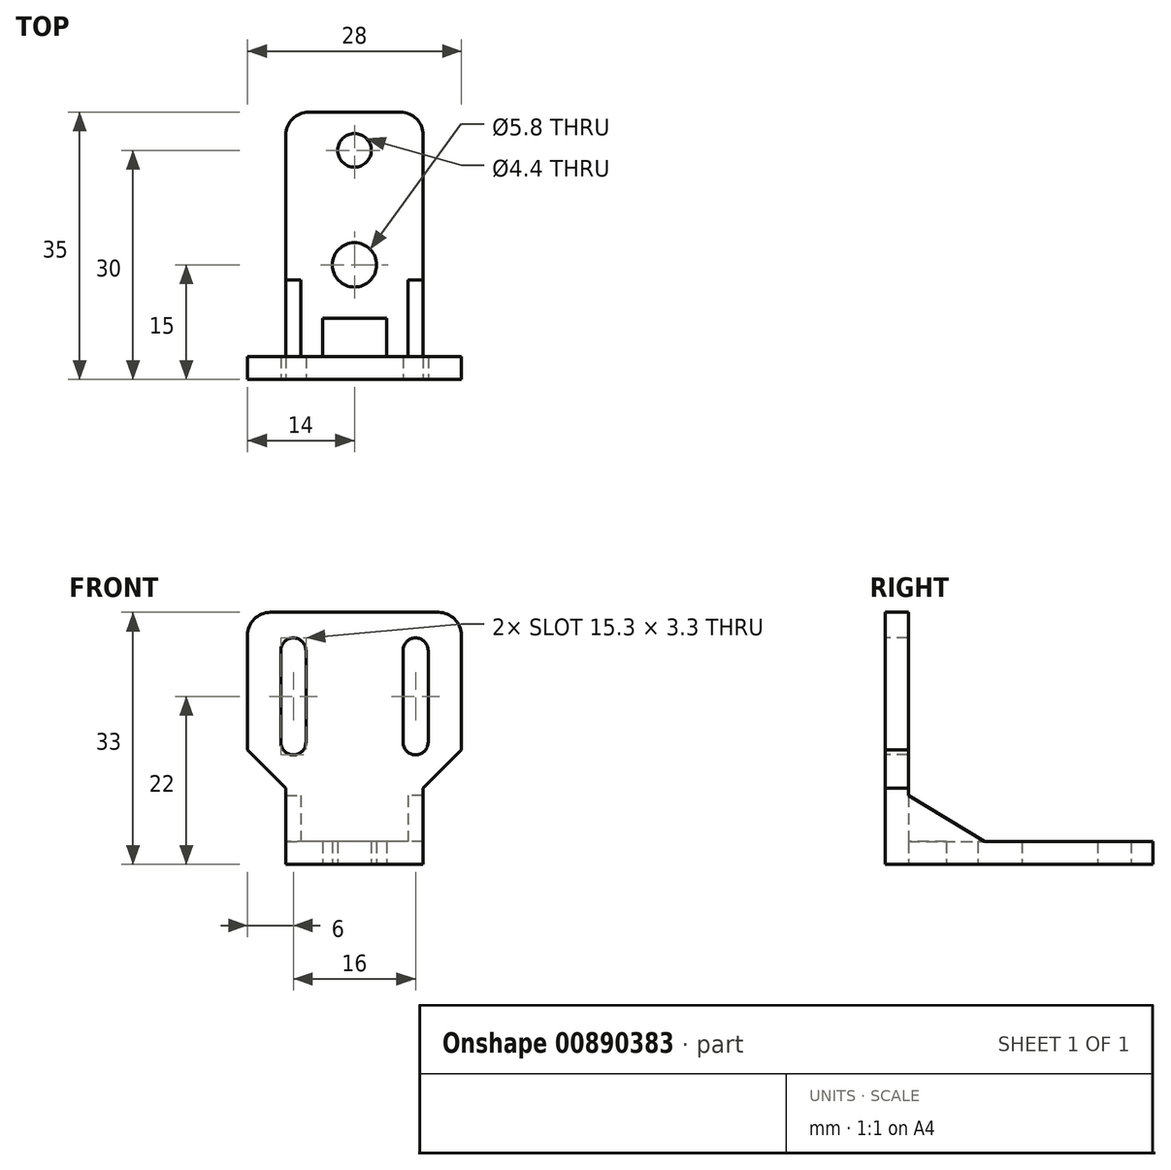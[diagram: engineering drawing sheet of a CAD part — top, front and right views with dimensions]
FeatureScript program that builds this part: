
annotation { "Feature Type Name" : "Feature", "Feature Type Description" : "" }
export const myFeature = defineFeature(function(context is Context, id is Id, definition is map)
    precondition{}
    {
        {
            var Q0;
            Q0=qCreatedBy(makeId("Top.planeOp"),FACE);
            var sketch = newSketch(context, id + "F0", { "sketchPlane" : qUnion([Q0])});
            skLineSegment(sketch, "E0.bottom", {"start": v(9, 17.5) * mm, "end": v(-9, 17.5) * mm});
            skLineSegment(sketch, "E0.top", {"start": v(9, -17.5) * mm, "end": v(-9, -17.5) * mm});
            skLineSegment(sketch, "E0.left", {"start": v(9, 17.5) * mm, "end": v(9, -17.5) * mm});
            skLineSegment(sketch, "E0.right", {"start": v(-9, 17.5) * mm, "end": v(-9, -17.5) * mm});
            skPoint(sketch, "E0.middle", {"position": v(0, 0) * mm});
            skCircle(sketch, "E1", {"center": v(0, 12.5) * mm, "radius": 2.2 * mm});
            skCircle(sketch, "E2", {"center": v(0, -2.5) * mm, "radius": 2.9 * mm});
            skLineSegment(sketch, "E3.bottom", {"start": v(4.2, -9.5) * mm, "end": v(-4.2, -9.5) * mm});
            skLineSegment(sketch, "E3.top", {"start": v(4.2, -14.5) * mm, "end": v(-4.2, -14.5) * mm});
            skLineSegment(sketch, "E3.left", {"start": v(4.2, -9.5) * mm, "end": v(4.2, -14.5) * mm});
            skLineSegment(sketch, "E3.right", {"start": v(-4.2, -9.5) * mm, "end": v(-4.2, -14.5) * mm});
            skPoint(sketch, "E3.middle", {"position": v(0, -12) * mm});
            skSolve(sketch);
        }
        {
            var Q0;
            Q0=makeQuery(id+"F0.imprint","IMPRINT",FACE,{"disambiguationData":[TD([[makeQuery(id+"F0.imprint","IMPRINT",EDGE,{"derivedFrom":sQuery(id+"F0.wireOp",EDGE,"E0.bottom")}),1.0]])]});
            extrude(context, id + "F1", {"entities" : qUnion([Q0]), "depth" : 3 * mm, "offsetDistance" : 25 * mm});
        }
        {
            var Q0;
            Q0=makeQuery(id+"F1.opExtrude","SWEPT_FACE",FACE,{"disambiguationData":[OSD([sQuery(id+"F0.wireOp",EDGE,"E0.top")])]});
            var sketch = newSketch(context, id + "F2", { "sketchPlane" : qUnion([Q0])});
            skLineSegment(sketch, "E4.bottom", {"start": v(-9, 0) * mm, "end": v(9, 0) * mm});
            skLineSegment(sketch, "E4.top", {"start": v(-9, 10) * mm, "end": v(9, 10) * mm});
            skLineSegment(sketch, "E4.left", {"start": v(-9, 0) * mm, "end": v(-9, 10) * mm});
            skLineSegment(sketch, "E4.right", {"start": v(9, 0) * mm, "end": v(9, 10) * mm});
            skLineSegment(sketch, "E5.bottom", {"start": v(14, 15) * mm, "end": v(-14, 15) * mm});
            skLineSegment(sketch, "E5.top", {"start": v(14, 33) * mm, "end": v(-14, 33) * mm});
            skLineSegment(sketch, "E5.left", {"start": v(14, 15) * mm, "end": v(14, 33) * mm});
            skLineSegment(sketch, "E5.right", {"start": v(-14, 15) * mm, "end": v(-14, 33) * mm});
            skPoint(sketch, "E5.middle", {"position": v(0, 24) * mm});
            skLineSegment(sketch, "E6", {"start": v(-14, 15) * mm, "end": v(-9, 10) * mm});
            skLineSegment(sketch, "E7", {"start": v(9, 10) * mm, "end": v(14, 15) * mm});
            skLineSegment(sketch, "E8", {"start": v(-8, 28) * mm, "end": v(-8, 16) * mm, "construction": true});
            skLineSegment(sketch, "E9.MirrorCS", {"start": v(8, 28) * mm, "end": v(8, 16) * mm, "construction": true});
            skArc(sketch, "E10.0.startCap", {"start": v(-9.65, 28) * mm, "mid": v(-8, 29.65) * mm, "end": v(-6.35, 28) * mm});
            skArc(sketch, "E10.0.endCap", {"start": v(-6.35, 16) * mm, "mid": v(-8, 14.35) * mm, "end": v(-9.65, 16) * mm});
            skLineSegment(sketch, "E10.0.left", {"start": v(-6.35, 28) * mm, "end": v(-6.35, 16) * mm});
            skLineSegment(sketch, "E10.0.right", {"start": v(-9.65, 28) * mm, "end": v(-9.65, 16) * mm});
            skArc(sketch, "E10.1.startCap", {"start": v(6.35, 28) * mm, "mid": v(8, 29.65) * mm, "end": v(9.65, 28) * mm});
            skArc(sketch, "E10.1.endCap", {"start": v(9.65, 16) * mm, "mid": v(8, 14.35) * mm, "end": v(6.35, 16) * mm});
            skLineSegment(sketch, "E10.1.left", {"start": v(9.65, 28) * mm, "end": v(9.65, 16) * mm});
            skLineSegment(sketch, "E10.1.right", {"start": v(6.35, 28) * mm, "end": v(6.35, 16) * mm});
            skSolve(sketch);
        }
        {
            var Q0;
            {var subQ0=sQuery(id+"F2.wireOp",EDGE,"E4.top");Q0=makeQuery(id+"F2.imprint","IMPRINT",FACE,{"disambiguationData":[TD([[makeQuery(id+"F2.imprint","IMPRINT",EDGE,{"derivedFrom":subQ0}),-1.0]])]});}
            var Q1;
            Q1=makeQuery(id+"F2.imprint","IMPRINT",FACE,{"disambiguationData":[TD([[makeQuery(id+"F2.imprint","IMPRINT",EDGE,{"derivedFrom":sQuery(id+"F2.wireOp",EDGE,"E4.top")}),1.0]])]});
            var Q2;
            Q2=makeQuery(id+"F2.imprint","IMPRINT",FACE,{"disambiguationData":[TD([[makeQuery(id+"F2.imprint","IMPRINT",EDGE,{"derivedFrom":sQuery(id+"F2.wireOp",EDGE,"E5.bottom")}),-1.0]])]});
            extrude(context, id + "F3", {"entities" : qUnion([Q0, Q1, Q2]), "operationType" : NewBodyOperationType.ADD, "oppositeDirection" : true, "depth" : 3 * mm, "offsetDistance" : 25 * mm});
        }
        {
            var Q0;
            Q0=qCreatedBy(makeId("Right.planeOp"),FACE);
            var sketch = newSketch(context, id + "F4", { "sketchPlane" : qUnion([Q0])});
            skLineSegment(sketch, "E11", {"start": v(-14.5, 9) * mm, "end": v(-4.5, 3) * mm});
            skLineSegment(sketch, "E12", {"start": v(-14.5, 9) * mm, "end": v(-14.5, 3) * mm});
            skLineSegment(sketch, "E13", {"start": v(-14.5, 3) * mm, "end": v(-4.5, 3) * mm});
            skSolve(sketch);
        }
        {
            var Q0;
            Q0=makeQuery(id+"F4.imprint","IMPRINT",FACE,{"disambiguationData":[TD([[makeQuery(id+"F4.imprint","IMPRINT",EDGE,{"derivedFrom":sQuery(id+"F4.wireOp",EDGE,"E11")}),-1.0]])]});
            var Q1;
            Q1=makeQuery(id+"F3.boolean.opBoolean","MERGE",FACE,{"derivedFrom":[makeQuery(id+"F1.opExtrude","SWEPT_FACE",FACE,{"disambiguationData":[OSD([sQuery(id+"F0.wireOp",EDGE,"E0.left")])]}),makeQuery(id+"F3.opExtrude","SWEPT_FACE",FACE,{"disambiguationData":[OSD([sQuery(id+"F2.wireOp",EDGE,"E4.right")])]})]});
            extrude(context, id + "F5", {"entities" : qUnion([Q0]), "operationType" : NewBodyOperationType.ADD, "endBound" : BoundingType.UP_TO_SURFACE, "depth" : 9.9 * mm, "endBoundEntityFace" : qUnion([Q1]), "offsetDistance" : 25 * mm, "hasSecondDirection" : true, "secondDirectionOppositeDirection" : false, "secondDirectionDepth" : 7 * mm});
        }
        {
            var Q0;
            Q0 = qSketchRegion(id + "F4", true);
            var Q1;
            Q1=makeQuery(id+"F3.boolean.opBoolean","MERGE",FACE,{"derivedFrom":[makeQuery(id+"F1.opExtrude","SWEPT_FACE",FACE,{"disambiguationData":[OSD([sQuery(id+"F0.wireOp",EDGE,"E0.right")])]}),makeQuery(id+"F3.opExtrude","SWEPT_FACE",FACE,{"disambiguationData":[OSD([sQuery(id+"F2.wireOp",EDGE,"E4.left")])]})]});
            extrude(context, id + "F6", {"entities" : qUnion([Q0]), "operationType" : NewBodyOperationType.ADD, "endBound" : BoundingType.UP_TO_SURFACE, "oppositeDirection" : true, "depth" : 20.8 * mm, "endBoundEntityFace" : qUnion([Q1]), "offsetDistance" : 25 * mm, "hasSecondDirection" : true, "secondDirectionOppositeDirection" : false, "secondDirectionDepth" : -7 * mm});
        }
        {
            var Q0;
            Q0=makeQuery(id+"F3.opExtrude","SWEPT_EDGE",EDGE,{"disambiguationData":[OSD([sQuery(id+"F2.wireOp",EDGE,"E5.top"),sQuery(id+"F2.wireOp",EDGE,"E5.right")])]});
            var Q1;
            Q1=makeQuery(id+"F3.opExtrude","SWEPT_EDGE",EDGE,{"disambiguationData":[OSD([sQuery(id+"F2.wireOp",EDGE,"E5.top"),sQuery(id+"F2.wireOp",EDGE,"E5.left")])]});
            var Q2;
            Q2=makeQuery(id+"F1.opExtrude","SWEPT_EDGE",EDGE,{"disambiguationData":[OSD([sQuery(id+"F0.wireOp",EDGE,"E0.bottom"),sQuery(id+"F0.wireOp",EDGE,"E0.left")])]});
            var Q3;
            Q3=makeQuery(id+"F1.opExtrude","SWEPT_EDGE",EDGE,{"disambiguationData":[OSD([sQuery(id+"F0.wireOp",EDGE,"E0.bottom"),sQuery(id+"F0.wireOp",EDGE,"E0.right")])]});
            fillet(context, id + "F7", {"entities" : qUnion([Q0, Q1, Q2, Q3]), "radius" : 3 * mm, "tangentPropagation" : true, "allowEdgeOverflow" : false});
        }
    });
